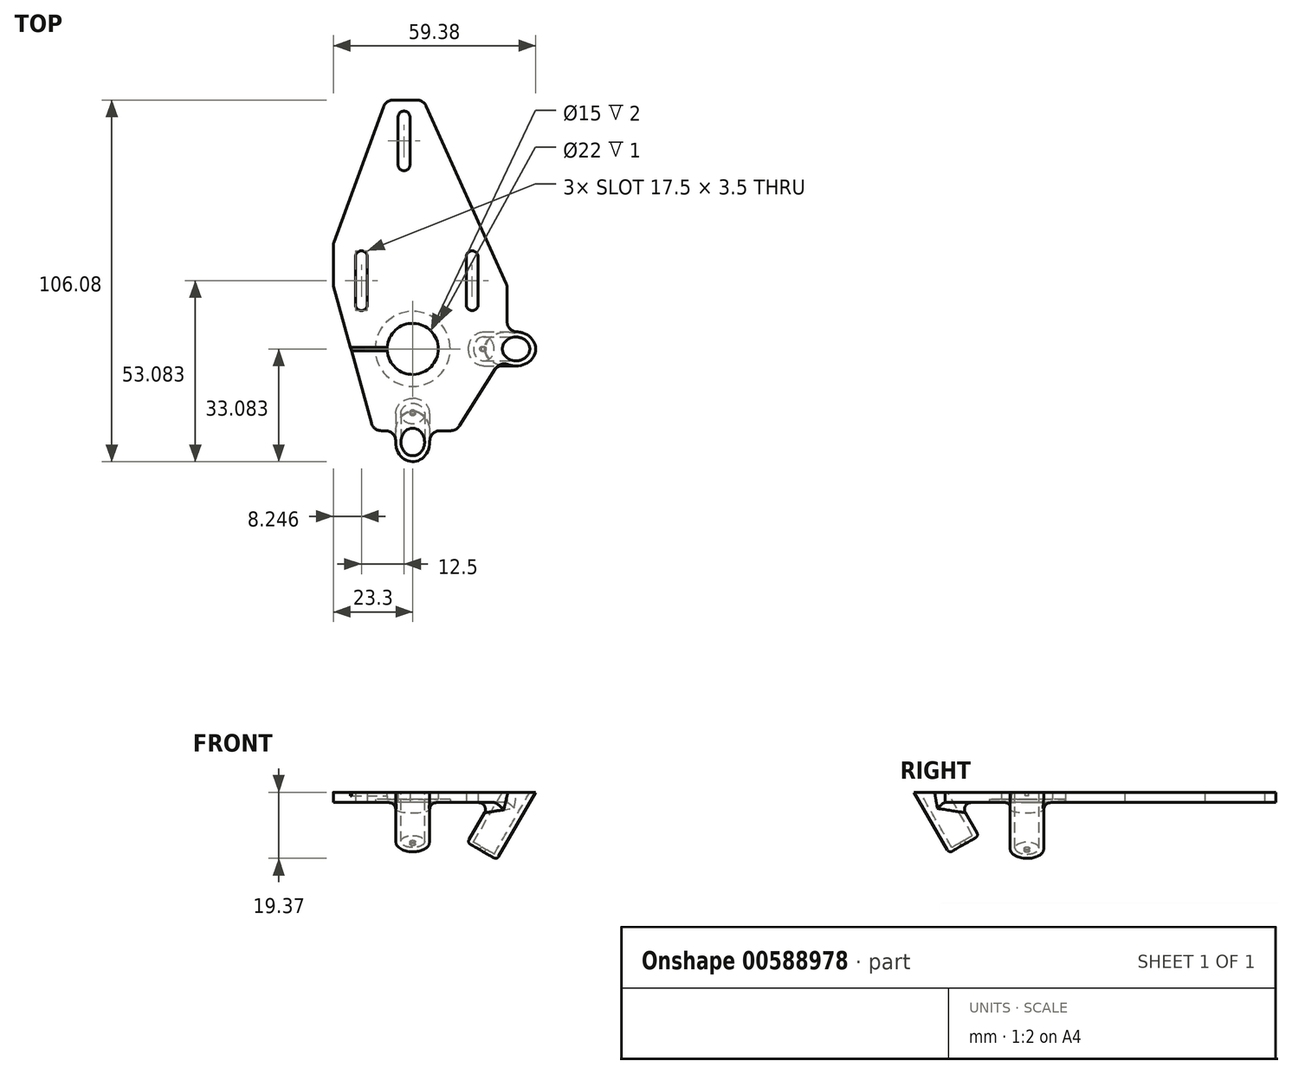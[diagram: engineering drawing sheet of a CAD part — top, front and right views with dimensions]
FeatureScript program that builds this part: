
annotation { "Feature Type Name" : "Feature", "Feature Type Description" : "" }
export const myFeature = defineFeature(function(context is Context, id is Id, definition is map)
    precondition{}
    {
        {
            var Q0;
            Q0=qCreatedBy(makeId("Top.planeOp"),FACE);
            var sketch = newSketch(context, id + "F0", { "sketchPlane" : qUnion([Q0])});
            skLineSegment(sketch, "E0", {"start": v(-23.76, -35) * mm, "end": v(-1.76, -35) * mm});
            skLineSegment(sketch, "E1", {"start": v(-1.76, -35) * mm, "end": v(14.2, -9.6) * mm});
            skLineSegment(sketch, "E2", {"start": v(14.2, -9.6) * mm, "end": v(14.2, 6.4) * mm});
            skLineSegment(sketch, "E3", {"start": v(14.2, 6.4) * mm, "end": v(-6.32, 52) * mm});
            skLineSegment(sketch, "E4", {"start": v(-6.32, 52) * mm, "end": v(-17.32, 52) * mm});
            skLineSegment(sketch, "E5", {"start": v(-17.32, 52) * mm, "end": v(-32.8, 9.74) * mm});
            skLineSegment(sketch, "E6", {"start": v(-32.8, 9.74) * mm, "end": v(-32.8, -2.23) * mm});
            skLineSegment(sketch, "E7", {"start": v(-32.8, -2.23) * mm, "end": v(-23.76, -35) * mm});
            skLineSegment(sketch, "E8", {"start": v(-32.8, 3.75) * mm, "end": v(14.2, 3.75) * mm, "construction": true});
            skLineSegment(sketch, "E9", {"start": v(-12.6, -35) * mm, "end": v(-12.6, 52) * mm, "construction": true});
            skCircle(sketch, "E10", {"center": v(-9.5, -21) * mm, "radius": 7.5 * mm});
            skLineSegment(sketch, "E11.bottom", {"start": v(-26.3, 6) * mm, "end": v(-22.8, 6) * mm});
            skLineSegment(sketch, "E11.top", {"start": v(-26.3, -8) * mm, "end": v(-22.8, -8) * mm});
            skLineSegment(sketch, "E11.left", {"start": v(-26.3, 6) * mm, "end": v(-26.3, -8) * mm});
            skLineSegment(sketch, "E11.right", {"start": v(-22.8, 6) * mm, "end": v(-22.8, -8) * mm});
            skLineSegment(sketch, "E12.bottom", {"start": v(6.2, -8) * mm, "end": v(9.7, -8) * mm});
            skLineSegment(sketch, "E12.top", {"start": v(6.2, 6) * mm, "end": v(9.7, 6) * mm});
            skLineSegment(sketch, "E12.left", {"start": v(6.2, -8) * mm, "end": v(6.2, 6) * mm});
            skLineSegment(sketch, "E12.right", {"start": v(9.7, -8) * mm, "end": v(9.7, 6) * mm});
            skLineSegment(sketch, "E13.bottom", {"start": v(-13.8, 47) * mm, "end": v(-10.3, 47) * mm});
            skLineSegment(sketch, "E13.top", {"start": v(-13.8, 33) * mm, "end": v(-10.3, 33) * mm});
            skLineSegment(sketch, "E13.left", {"start": v(-13.8, 47) * mm, "end": v(-13.8, 33) * mm});
            skLineSegment(sketch, "E13.right", {"start": v(-10.3, 47) * mm, "end": v(-10.3, 33) * mm});
            skArc(sketch, "E14", {"start": v(-10.3, 47) * mm, "mid": v(-12.05, 48.74) * mm, "end": v(-13.8, 47) * mm});
            skArc(sketch, "E15", {"start": v(-13.8, 33) * mm, "mid": v(-12.05, 31.24) * mm, "end": v(-10.3, 33) * mm});
            skArc(sketch, "E16", {"start": v(-22.8, 6) * mm, "mid": v(-24.55, 7.74) * mm, "end": v(-26.3, 6) * mm});
            skArc(sketch, "E17", {"start": v(9.7, 6) * mm, "mid": v(7.95, 7.74) * mm, "end": v(6.2, 6) * mm});
            skArc(sketch, "E18", {"start": v(-26.3, -8) * mm, "mid": v(-24.55, -9.76) * mm, "end": v(-22.8, -8) * mm});
            skArc(sketch, "E19", {"start": v(6.2, -8) * mm, "mid": v(7.95, -9.76) * mm, "end": v(9.7, -8) * mm});
            skLineSegment(sketch, "E20", {"start": v(-32.8, 9.74) * mm, "end": v(-32.8, 64.13) * mm, "construction": true});
            skCircle(sketch, "E21", {"center": v(-9.5, -21) * mm, "radius": 11 * mm});
            skLineSegment(sketch, "E22", {"start": v(14.2, -9.6) * mm, "end": v(14.2, -35) * mm});
            skLineSegment(sketch, "E23", {"start": v(14.2, -35) * mm, "end": v(-1.76, -35) * mm});
            skLineSegment(sketch, "E24", {"start": v(-9.5, -21) * mm, "end": v(55.84, -21) * mm, "construction": true});
            skLineSegment(sketch, "E25", {"start": v(-9.5, -21) * mm, "end": v(-9.5, -68.26) * mm, "construction": true});
            skLineSegment(sketch, "E26", {"start": v(-23.76, -35) * mm, "end": v(-21, -45) * mm});
            skLineSegment(sketch, "E27", {"start": v(-21, -45) * mm, "end": v(14.2, -45) * mm});
            skLineSegment(sketch, "E28", {"start": v(14.2, -45) * mm, "end": v(14.2, -35) * mm});
            skLineSegment(sketch, "E29", {"start": v(3.34, -45) * mm, "end": v(14.2, -27.72) * mm});
            skLineSegment(sketch, "E30.bottom", {"start": v(-30.55, -20.5) * mm, "end": v(-9.5, -20.5) * mm});
            skLineSegment(sketch, "E30.top", {"start": v(-30.55, -21.5) * mm, "end": v(-9.5, -21.5) * mm});
            skLineSegment(sketch, "E30.left", {"start": v(-30.55, -20.5) * mm, "end": v(-30.55, -21.5) * mm});
            skLineSegment(sketch, "E30.right", {"start": v(-9.5, -20.5) * mm, "end": v(-9.5, -21.5) * mm});
            skLineSegment(sketch, "E31", {"start": v(14.2, -27.72) * mm, "end": v(18.2, -21.35) * mm});
            skLineSegment(sketch, "E32", {"start": v(18.2, -21.35) * mm, "end": v(18.2, -2.5) * mm});
            skLineSegment(sketch, "E33", {"start": v(18.2, -2.5) * mm, "end": v(14.2, 6.4) * mm});
            skSolve(sketch);
        }
        {
            var Q0;
            Q0=makeQuery(id+"F0.imprint","IMPRINT",FACE,{"disambiguationData":[TD([[makeQuery(id+"F0.imprint","IMPRINT",EDGE,{"derivedFrom":sQuery(id+"F0.wireOp",EDGE,"E0")}),1.0]])]});
            var Q1;
            Q1=makeQuery(id+"F0.imprint","IMPRINT",FACE,{"disambiguationData":[TD([[makeQuery(id+"F0.imprint","IMPRINT",EDGE,{"derivedFrom":sQuery(id+"F0.wireOp",EDGE,"E10")}),-1.0]])]});
            var Q2;
            Q2=makeQuery(id+"F0.imprint","IMPRINT",FACE,{"disambiguationData":[TD([[makeQuery(id+"F0.imprint","IMPRINT",EDGE,{"derivedFrom":sQuery(id+"F0.wireOp",EDGE,"E1")}),-1.0]])]});
            var Q3;
            Q3=makeQuery(id+"F0.imprint","IMPRINT",FACE,{"disambiguationData":[TD([[makeQuery(id+"F0.imprint","IMPRINT",EDGE,{"derivedFrom":sQuery(id+"F0.wireOp",EDGE,"E0")}),-1.0]])]});
            var Q4;
            {var subQ0=sQuery(id+"F0.wireOp",EDGE,"E30.bottom");var subQ1=sQuery(id+"F0.wireOp",EDGE,"E7");var subQ2=makeQuery(id+"F0.imprint","INTERSECT",VERTEX,{"derivedFrom":[subQ1,subQ0]});Q4=makeQuery(id+"F0.imprint","IMPRINT",FACE,{"disambiguationData":[TD([[makeQuery(id+"F0.imprint","IMPRINT",EDGE,{"disambiguationData":[TD([[subQ2,-1.0]])],"derivedFrom":subQ1}),1.0]])]});}
            var Q5;
            {var subQ2=sQuery(id+"F0.wireOp",EDGE,"E2");Q5=makeQuery(id+"F0.imprint","IMPRINT",FACE,{"disambiguationData":[TD([[makeQuery(id+"F0.imprint","IMPRINT",EDGE,{"derivedFrom":subQ2}),-1.0]])]});}
            extrude(context, id + "F1", {"entities" : qUnion([Q0, Q1, Q2, Q3, Q4, Q5]), "depth" : 3 * mm, "offsetDistance" : 25 * mm});
        }
        {
            var Q0;
            Q0=makeQuery(id+"F0.imprint","IMPRINT",FACE,{"disambiguationData":[TD([[makeQuery(id+"F0.imprint","IMPRINT",EDGE,{"derivedFrom":sQuery(id+"F0.wireOp",EDGE,"E10")}),-1.0]])]});
            extrude(context, id + "F2", {"entities" : qUnion([Q0]), "operationType" : NewBodyOperationType.REMOVE, "depth" : 1 * mm, "offsetDistance" : 25 * mm});
        }
        {
            var Q0;
            Q0=qCreatedBy(makeId("Top.planeOp"),FACE);
            cPlane(context, id + "F3", {"entities" : qUnion([Q0]), "cplaneType" : CPlaneType.OFFSET, "offset" : 49.5 * mm, "oppositeDirection" : true, "width" : 150 * mm, "height" : 150 * mm});
        }
        {
            var Q0;
            Q0=qCreatedBy(id+"F3.planeOp",FACE);
            var sketch = newSketch(context, id + "F4", { "sketchPlane" : qUnion([Q0])});
            skPoint(sketch, "E34", {"position": v(-9.5, -21) * mm});
            skPoint(sketch, "E35", {"position": v(-9.5, -18) * mm});
            skSolve(sketch);
        }
        {
            var Q0;
            Q0=sQuery(id+"F0.wireOp",EDGE,"E32");
            cPlane(context, id + "F5", {"entities" : qUnion([Q0]), "cplaneType" : CPlaneType.LINE_ANGLE, "offset" : 25 * mm, "angle" : 30 * degree, "width" : 150 * mm, "height" : 150 * mm});
        }
        {
            var Q0;
            Q0=makeQuery(id+"F1.opExtrude","CAP_EDGE",EDGE,{"disambiguationData":[OSD([sQuery(id+"F0.wireOp",EDGE,"E27")])],"isStart":false});
            cPlane(context, id + "F6", {"entities" : qUnion([Q0]), "cplaneType" : CPlaneType.LINE_ANGLE, "offset" : 25 * mm, "angle" : 60 * degree, "oppositeDirection" : true, "width" : 150 * mm, "height" : 150 * mm});
        }
        {
            var Q0;
            Q0=qCreatedBy(id+"F6.planeOp",FACE);
            var sketch = newSketch(context, id + "F7", { "sketchPlane" : qUnion([Q0])});
            skCircle(sketch, "E36", {"center": v(-9.5, 40.34) * mm, "radius": 3.5 * mm});
            skCircle(sketch, "E37", {"center": v(-9.5, 40.34) * mm, "radius": 5 * mm});
            skSolve(sketch);
        }
        {
            var Q0;
            Q0=qCreatedBy(id+"F5.planeOp",FACE);
            var sketch = newSketch(context, id + "F8", { "sketchPlane" : qUnion([Q0])});
            skCircle(sketch, "E38", {"center": v(16.52, -21) * mm, "radius": 3.5 * mm});
            skCircle(sketch, "E39", {"center": v(16.52, -21) * mm, "radius": 5 * mm});
            skSolve(sketch);
        }
        {
            var Q0;
            Q0=makeQuery(id+"F7.imprint","IMPRINT",FACE,{"disambiguationData":[TD([[makeQuery(id+"F7.imprint","IMPRINT",EDGE,{"derivedFrom":sQuery(id+"F7.wireOp",EDGE,"E36")}),-1.0]])]});
            extrude(context, id + "F9", {"entities" : qUnion([Q0]), "operationType" : NewBodyOperationType.ADD, "depth" : 15 * mm, "offsetDistance" : 25 * mm});
        }
        {
            var Q0;
            Q0=makeQuery(id+"F8.imprint","IMPRINT",FACE,{"disambiguationData":[TD([[makeQuery(id+"F8.imprint","IMPRINT",EDGE,{"derivedFrom":sQuery(id+"F8.wireOp",EDGE,"E38")}),-1.0]])]});
            extrude(context, id + "F10", {"entities" : qUnion([Q0]), "operationType" : NewBodyOperationType.ADD, "oppositeDirection" : true, "depth" : 15 * mm, "offsetDistance" : 25 * mm});
        }
        {
            var Q0;
            Q0=makeQuery(id+"F7.imprint","IMPRINT",FACE,{"disambiguationData":[TD([[makeQuery(id+"F7.imprint","IMPRINT",EDGE,{"derivedFrom":sQuery(id+"F7.wireOp",EDGE,"E36")}),1.0]])]});
            extrude(context, id + "F11", {"entities" : qUnion([Q0]), "operationType" : NewBodyOperationType.REMOVE, "depth" : 10 * mm, "offsetDistance" : 25 * mm});
        }
        {
            var Q0;
            Q0=makeQuery(id+"F8.imprint","IMPRINT",FACE,{"disambiguationData":[TD([[makeQuery(id+"F8.imprint","IMPRINT",EDGE,{"derivedFrom":sQuery(id+"F8.wireOp",EDGE,"E38")}),1.0]])]});
            extrude(context, id + "F12", {"entities" : qUnion([Q0]), "operationType" : NewBodyOperationType.REMOVE, "oppositeDirection" : true, "depth" : 5 * mm, "offsetDistance" : 25 * mm});
        }
        {
            var Q0;
            Q0=makeQuery(id+"F10.opExtrude","CAP_FACE",FACE,{"disambiguationData":[OSD([sQuery(id+"F8.wireOp",EDGE,"E38"),sQuery(id+"F8.wireOp",EDGE,"E39")])],"isStart":true});
            var Q1;
            Q1=makeQuery(id+"F8.imprint","IMPRINT",FACE,{"disambiguationData":[TD([[makeQuery(id+"F8.imprint","IMPRINT",EDGE,{"derivedFrom":sQuery(id+"F8.wireOp",EDGE,"E38")}),-1.0]])]});
            extrude(context, id + "F13", {"entities" : qUnion([Q0, Q1]), "operationType" : NewBodyOperationType.ADD, "depth" : 7 * mm, "offsetDistance" : 25 * mm});
        }
        {
            var Q0;
            Q0=makeQuery(id+"F9.opExtrude","CAP_FACE",FACE,{"disambiguationData":[OSD([sQuery(id+"F7.wireOp",EDGE,"E36"),sQuery(id+"F7.wireOp",EDGE,"E37")])],"isStart":true});
            extrude(context, id + "F14", {"entities" : qUnion([Q0]), "operationType" : NewBodyOperationType.ADD, "depth" : 5 * mm, "offsetDistance" : 25 * mm});
        }
        {
            var Q0;
            Q0=makeQuery(id+"F1.opExtrude","SWEPT_FACE",FACE,{"disambiguationData":[OSD([sQuery(id+"F0.wireOp",EDGE,"E7"),sQuery(id+"F0.wireOp",EDGE,"E26")])]});
            var sketch = newSketch(context, id + "F15", { "sketchPlane" : qUnion([Q0])});
            skLineSegment(sketch, "E40.bottom", {"start": v(-6.57, 3) * mm, "end": v(71.8, 3) * mm});
            skLineSegment(sketch, "E40.top", {"start": v(-6.57, 11.39) * mm, "end": v(71.8, 11.39) * mm});
            skLineSegment(sketch, "E40.left", {"start": v(-6.57, 3) * mm, "end": v(-6.57, 11.39) * mm});
            skLineSegment(sketch, "E40.right", {"start": v(71.8, 3) * mm, "end": v(71.8, 11.39) * mm});
            skSolve(sketch);
        }
        {
            var Q0;
            Q0=makeQuery(id+"F15.imprint","IMPRINT",FACE,{"disambiguationData":[TD([[makeQuery(id+"F15.imprint","IMPRINT",EDGE,{"derivedFrom":sQuery(id+"F15.wireOp",EDGE,"E40.top")}),-1.0]])]});
            extrude(context, id + "F16", {"entities" : qUnion([Q0]), "operationType" : NewBodyOperationType.REMOVE, "oppositeDirection" : true, "depth" : 60 * mm, "offsetDistance" : 25 * mm});
        }
        {
            var Q0;
            Q0=makeQuery(id+"F10.opExtrude","CAP_FACE",FACE,{"disambiguationData":[OSD([sQuery(id+"F8.wireOp",EDGE,"E38"),sQuery(id+"F8.wireOp",EDGE,"E39")])],"isStart":false});
            var sketch = newSketch(context, id + "F17", { "sketchPlane" : qUnion([Q0])});
            skCircle(sketch, "E41", {"center": v(16.52, 21) * mm, "radius": 5 * mm});
            skCircle(sketch, "E42", {"center": v(16.52, 21) * mm, "radius": 0.75 * mm});
            skSolve(sketch);
        }
        {
            var Q0;
            Q0=makeQuery(id+"F17.imprint","IMPRINT",FACE,{"disambiguationData":[TD([[makeQuery(id+"F17.imprint","IMPRINT",EDGE,{"derivedFrom":sQuery(id+"F17.wireOp",EDGE,"E42")}),-1.0]])]});
            var Q1;
            Q1=makeQuery(id+"F17.imprint","IMPRINT",FACE,{"disambiguationData":[TD([[makeQuery(id+"F17.imprint","IMPRINT",EDGE,{"derivedFrom":sQuery(id+"F17.wireOp",EDGE,"E41")}),-1.0]])]});
            extrude(context, id + "F18", {"entities" : qUnion([Q0, Q1]), "operationType" : NewBodyOperationType.ADD, "depth" : 1 * mm, "offsetDistance" : 25 * mm});
        }
        {
            var Q0;
            Q0=makeQuery(id+"F9.opExtrude","CAP_FACE",FACE,{"disambiguationData":[OSD([sQuery(id+"F7.wireOp",EDGE,"E36"),sQuery(id+"F7.wireOp",EDGE,"E37")])],"isStart":false});
            var sketch = newSketch(context, id + "F19", { "sketchPlane" : qUnion([Q0])});
            skCircle(sketch, "E43", {"center": v(-9.5, 40.34) * mm, "radius": 5 * mm});
            skCircle(sketch, "E44", {"center": v(-9.5, 40.34) * mm, "radius": 0.75 * mm});
            skSolve(sketch);
        }
        {
            var Q0;
            Q0=makeQuery(id+"F19.imprint","IMPRINT",FACE,{"disambiguationData":[TD([[makeQuery(id+"F19.imprint","IMPRINT",EDGE,{"derivedFrom":sQuery(id+"F19.wireOp",EDGE,"E44")}),-1.0]])]});
            var Q1;
            Q1=makeQuery(id+"F19.imprint","IMPRINT",FACE,{"disambiguationData":[TD([[makeQuery(id+"F19.imprint","IMPRINT",EDGE,{"derivedFrom":sQuery(id+"F19.wireOp",EDGE,"E43")}),1.0]])]});
            extrude(context, id + "F20", {"entities" : qUnion([Q0, Q1]), "operationType" : NewBodyOperationType.ADD, "depth" : 1 * mm, "offsetDistance" : 25 * mm});
        }
        {
            var Q0;
            Q0=makeQuery(id+"F1.opExtrude","SWEPT_EDGE",EDGE,{"disambiguationData":[OSD([sQuery(id+"F0.wireOp",EDGE,"E27"),sQuery(id+"F0.wireOp",EDGE,"E29")])]});
            var Q1;
            Q1=makeQuery(id+"F1.opExtrude","SWEPT_EDGE",EDGE,{"disambiguationData":[OSD([sQuery(id+"F0.wireOp",EDGE,"E26"),sQuery(id+"F0.wireOp",EDGE,"E27")])]});
            var Q2;
            Q2=makeQuery(id+"F1.opExtrude","SWEPT_EDGE",EDGE,{"disambiguationData":[OSD([sQuery(id+"F0.wireOp",EDGE,"E22"),sQuery(id+"F0.wireOp",EDGE,"E29")])]});
            var Q3;
            Q3=makeQuery(id+"F1.opExtrude","SWEPT_EDGE",EDGE,{"disambiguationData":[OSD([sQuery(id+"F0.wireOp",EDGE,"E6"),sQuery(id+"F0.wireOp",EDGE,"E7")])]});
            var Q4;
            Q4=makeQuery(id+"F1.opExtrude","SWEPT_EDGE",EDGE,{"disambiguationData":[OSD([sQuery(id+"F0.wireOp",EDGE,"E2"),sQuery(id+"F0.wireOp",EDGE,"E3")])]});
            var Q5;
            Q5=makeQuery(id+"F1.opExtrude","SWEPT_EDGE",EDGE,{"disambiguationData":[OSD([sQuery(id+"F0.wireOp",EDGE,"E3"),sQuery(id+"F0.wireOp",EDGE,"E4")])]});
            var Q6;
            Q6=makeQuery(id+"F1.opExtrude","SWEPT_EDGE",EDGE,{"disambiguationData":[OSD([sQuery(id+"F0.wireOp",EDGE,"E4"),sQuery(id+"F0.wireOp",EDGE,"E5")])]});
            var Q7;
            Q7=makeQuery(id+"F1.opExtrude","SWEPT_EDGE",EDGE,{"disambiguationData":[OSD([sQuery(id+"F0.wireOp",EDGE,"E5"),sQuery(id+"F0.wireOp",EDGE,"E6")])]});
            var Q8;
            Q8=makeQuery(id+"F1.opExtrude","SWEPT_EDGE",EDGE,{"disambiguationData":[OSD([sQuery(id+"F0.wireOp",EDGE,"E32"),sQuery(id+"F0.wireOp",EDGE,"E33")])]});
            var Q9;
            {var subQ0=sQuery(id+"F8.wireOp",EDGE,"E39");Q9=makeQuery(id+"F13.boolean.opBoolean","INTERSECT",EDGE,{"derivedFrom":[makeQuery(id+"F1.opExtrude","SWEPT_FACE",FACE,{"disambiguationData":[OSD([sQuery(id+"F0.wireOp",EDGE,"E32")])]}),makeQuery(id+"F13.opExtrude","SWEPT_FACE",FACE,{"disambiguationData":[OSD([subQ0]),TDD([makeQuery(id+"F8.imprint","IMPRINT",EDGE,{"derivedFrom":subQ0})])]})]});}
            var Q10;
            {var subQ0=sQuery(id+"F8.wireOp",EDGE,"E39");Q10=makeQuery(id+"F13.boolean.opBoolean","INTERSECT",EDGE,{"derivedFrom":[makeQuery(id+"F1.opExtrude","SWEPT_FACE",FACE,{"disambiguationData":[OSD([sQuery(id+"F0.wireOp",EDGE,"E29"),sQuery(id+"F0.wireOp",EDGE,"E31")])]}),makeQuery(id+"F13.opExtrude","SWEPT_FACE",FACE,{"disambiguationData":[OSD([subQ0]),TDD([makeQuery(id+"F8.imprint","IMPRINT",EDGE,{"derivedFrom":subQ0})])]})]});}
            var Q11;
            Q11=makeQuery(id+"F9.boolean.opBoolean","INTERSECT",EDGE,{"disambiguationData":[OD(1.0)],"derivedFrom":[makeQuery(id+"F1.opExtrude","SWEPT_FACE",FACE,{"disambiguationData":[OSD([sQuery(id+"F0.wireOp",EDGE,"E27")])]}),makeQuery(id+"F9.opExtrude","SWEPT_FACE",FACE,{"disambiguationData":[OSD([sQuery(id+"F7.wireOp",EDGE,"E37")])]})]});
            var Q12;
            Q12=makeQuery(id+"F9.boolean.opBoolean","INTERSECT",EDGE,{"disambiguationData":[OD(0.0)],"derivedFrom":[makeQuery(id+"F1.opExtrude","SWEPT_FACE",FACE,{"disambiguationData":[OSD([sQuery(id+"F0.wireOp",EDGE,"E27")])]}),makeQuery(id+"F9.opExtrude","SWEPT_FACE",FACE,{"disambiguationData":[OSD([sQuery(id+"F7.wireOp",EDGE,"E37")])]})]});
            fillet(context, id + "F21", {"entities" : qUnion([Q0, Q1, Q2, Q3, Q4, Q5, Q6, Q7, Q8, Q9, Q10, Q11, Q12]), "radius" : 3 * mm, "tangentPropagation" : true, "allowEdgeOverflow" : false});
        }
        {
            var Q0;
            {var subQ0=sQuery(id+"F0.wireOp",EDGE,"E12.right");var subQ1=sQuery(id+"F0.wireOp",EDGE,"E12.left");var subQ2=sQuery(id+"F0.wireOp",EDGE,"E11.right");var subQ3=sQuery(id+"F0.wireOp",EDGE,"E11.left");var subQ4=sQuery(id+"F0.wireOp",EDGE,"E26");var subQ5=sQuery(id+"F0.wireOp",EDGE,"E7");var subQ6=sQuery(id+"F0.wireOp",EDGE,"E6");var subQ7=sQuery(id+"F0.wireOp",EDGE,"E22");var subQ8=sQuery(id+"F0.wireOp",EDGE,"E2");var subQ9=sQuery(id+"F0.wireOp",EDGE,"E3");var subQ10=sQuery(id+"F0.wireOp",EDGE,"E4");var subQ11=sQuery(id+"F0.wireOp",EDGE,"E5");var subQ12=sQuery(id+"F0.wireOp",EDGE,"E13.left");var subQ13=sQuery(id+"F0.wireOp",EDGE,"E13.right");var subQ14=sQuery(id+"F0.wireOp",EDGE,"E14");var subQ15=sQuery(id+"F0.wireOp",EDGE,"E15");var subQ16=sQuery(id+"F0.wireOp",EDGE,"E16");var subQ17=sQuery(id+"F0.wireOp",EDGE,"E17");var subQ18=sQuery(id+"F0.wireOp",EDGE,"E18");var subQ19=sQuery(id+"F0.wireOp",EDGE,"E19");var subQ20=sQuery(id+"F0.wireOp",EDGE,"E27");var subQ21=sQuery(id+"F0.wireOp",EDGE,"E29");Q0=makeQuery(id+"F10.boolean.opBoolean","INTERSECT",EDGE,{"derivedFrom":[makeQuery(id+"F9.boolean.opBoolean","SPLIT",FACE,{"disambiguationData":[TD([makeQuery(id+"F1.opExtrude","SWEPT_FACE",FACE,{"disambiguationData":[OSD([subQ9])]})])],"derivedFrom":makeQuery(id+"F1.opExtrude","CAP_FACE",FACE,{"disambiguationData":[OSD([subQ8,subQ9,subQ10,subQ11,subQ6,subQ5,sQuery(id+"F0.wireOp",EDGE,"E10"),subQ3,subQ2,subQ1,subQ0,subQ12,subQ13,subQ14,subQ15,subQ16,subQ17,subQ18,subQ19,subQ7,subQ4,subQ20,subQ21])],"isStart":true})}),makeQuery(id+"F10.opExtrude","SWEPT_FACE",FACE,{"disambiguationData":[OSD([sQuery(id+"F8.wireOp",EDGE,"E39")])]})]});}
            var Q1;
            Q1=makeQuery(id+"F9.boolean.opBoolean","INTERSECT",EDGE,{"derivedFrom":[makeQuery(id+"F1.opExtrude","CAP_FACE",FACE,{"disambiguationData":[OSD([sQuery(id+"F0.wireOp",EDGE,"E2"),sQuery(id+"F0.wireOp",EDGE,"E3"),sQuery(id+"F0.wireOp",EDGE,"E4"),sQuery(id+"F0.wireOp",EDGE,"E5"),sQuery(id+"F0.wireOp",EDGE,"E6"),sQuery(id+"F0.wireOp",EDGE,"E7"),sQuery(id+"F0.wireOp",EDGE,"E10"),sQuery(id+"F0.wireOp",EDGE,"E11.left"),sQuery(id+"F0.wireOp",EDGE,"E11.right"),sQuery(id+"F0.wireOp",EDGE,"E12.left"),sQuery(id+"F0.wireOp",EDGE,"E12.right"),sQuery(id+"F0.wireOp",EDGE,"E13.left"),sQuery(id+"F0.wireOp",EDGE,"E13.right"),sQuery(id+"F0.wireOp",EDGE,"E14"),sQuery(id+"F0.wireOp",EDGE,"E15"),sQuery(id+"F0.wireOp",EDGE,"E16"),sQuery(id+"F0.wireOp",EDGE,"E17"),sQuery(id+"F0.wireOp",EDGE,"E18"),sQuery(id+"F0.wireOp",EDGE,"E19"),sQuery(id+"F0.wireOp",EDGE,"E22"),sQuery(id+"F0.wireOp",EDGE,"E26"),sQuery(id+"F0.wireOp",EDGE,"E27"),sQuery(id+"F0.wireOp",EDGE,"E29")])],"isStart":true}),makeQuery(id+"F9.opExtrude","SWEPT_FACE",FACE,{"disambiguationData":[OSD([sQuery(id+"F7.wireOp",EDGE,"E37")])]})]});
            fillet(context, id + "F22", {"entities" : qUnion([Q0, Q1]), "radius" : 2 * mm, "tangentPropagation" : true, "allowEdgeOverflow" : false});
        }
        {
            var Q0;
            Q0=makeQuery(id+"F20.opExtrude","CAP_EDGE",EDGE,{"disambiguationData":[OSD([sQuery(id+"F19.wireOp",EDGE,"E43")])],"isStart":false});
            var Q1;
            Q1=makeQuery(id+"F18.opExtrude","CAP_EDGE",EDGE,{"disambiguationData":[OSD([sQuery(id+"F17.wireOp",EDGE,"E41")])],"isStart":false});
            fillet(context, id + "F23", {"entities" : qUnion([Q0, Q1]), "radius" : 1 * mm, "tangentPropagation" : true, "allowEdgeOverflow" : false});
        }
        {
            var Q0;
            {var subQ0=sQuery(id+"F0.wireOp",EDGE,"E29");var subQ2=sQuery(id+"F0.wireOp",EDGE,"E27");var subQ4=sQuery(id+"F0.wireOp",EDGE,"E19");var subQ6=sQuery(id+"F0.wireOp",EDGE,"E18");var subQ8=sQuery(id+"F0.wireOp",EDGE,"E17");var subQ10=sQuery(id+"F0.wireOp",EDGE,"E16");var subQ12=sQuery(id+"F0.wireOp",EDGE,"E15");var subQ14=sQuery(id+"F0.wireOp",EDGE,"E14");var subQ16=sQuery(id+"F0.wireOp",EDGE,"E13.right");var subQ18=sQuery(id+"F0.wireOp",EDGE,"E13.left");var subQ20=sQuery(id+"F0.wireOp",EDGE,"E12.right");var subQ22=sQuery(id+"F0.wireOp",EDGE,"E5");var subQ24=sQuery(id+"F0.wireOp",EDGE,"E4");var subQ26=sQuery(id+"F0.wireOp",EDGE,"E3");var subQ27=makeQuery(id+"F1.opExtrude","SWEPT_FACE",FACE,{"disambiguationData":[OSD([subQ26])]});var subQ28=sQuery(id+"F0.wireOp",EDGE,"E22");var subQ29=sQuery(id+"F0.wireOp",EDGE,"E2");var subQ31=sQuery(id+"F0.wireOp",EDGE,"E6");var subQ33=sQuery(id+"F0.wireOp",EDGE,"E26");var subQ34=sQuery(id+"F0.wireOp",EDGE,"E7");var subQ38=sQuery(id+"F0.wireOp",EDGE,"E10");var subQ40=sQuery(id+"F0.wireOp",EDGE,"E11.left");var subQ42=sQuery(id+"F0.wireOp",EDGE,"E11.right");var subQ44=sQuery(id+"F0.wireOp",EDGE,"E12.left");Q0=makeQuery(id+"F16.boolean.opBoolean","MERGE",FACE,{"derivedFrom":[makeQuery(id+"F10.boolean.opBoolean","SPLIT",FACE,{"disambiguationData":[TD([subQ27])],"derivedFrom":makeQuery(id+"F9.boolean.opBoolean","SPLIT",FACE,{"disambiguationData":[TD([subQ27])],"derivedFrom":makeQuery(id+"F1.opExtrude","CAP_FACE",FACE,{"disambiguationData":[OSD([subQ29,subQ26,subQ24,subQ22,subQ31,subQ34,subQ38,subQ40,subQ42,subQ44,subQ20,subQ18,subQ16,subQ14,subQ12,subQ10,subQ8,subQ6,subQ4,subQ28,subQ33,subQ2,subQ0])],"isStart":false})})}),makeQuery(id+"F16.opExtrude","SWEPT_FACE",FACE,{"disambiguationData":[OSD([sQuery(id+"F15.wireOp",EDGE,"E40.bottom")])]})]});}
            var sketch = newSketch(context, id + "F24", { "sketchPlane" : qUnion([Q0])});
            skLineSegment(sketch, "E45.bottom", {"start": v(-30.55, -20.5) * mm, "end": v(-9.5, -20.5) * mm});
            skLineSegment(sketch, "E45.top", {"start": v(-30.55, -21.5) * mm, "end": v(-9.5, -21.5) * mm});
            skLineSegment(sketch, "E45.left", {"start": v(-30.55, -20.5) * mm, "end": v(-30.55, -21.5) * mm});
            skLineSegment(sketch, "E45.right", {"start": v(-9.5, -20.5) * mm, "end": v(-9.5, -21.5) * mm});
            skSolve(sketch);
        }
        {
            var Q0;
            {var subQ0=sQuery(id+"F24.wireOp",EDGE,"E45.bottom");var subQ3=makeQuery(id+"F1.opExtrude","CAP_EDGE",EDGE,{"disambiguationData":[OSD([sQuery(id+"F0.wireOp",EDGE,"E10")])],"isStart":false});var subQ4=makeQuery(id+"F24.imprint","INTERSECT",VERTEX,{"derivedFrom":[subQ3,subQ0]});Q0=makeQuery(id+"F24.imprint","IMPRINT",FACE,{"disambiguationData":[TD([[makeQuery(id+"F24.imprint","IMPRINT",EDGE,{"disambiguationData":[TD([[subQ4,-1.0]])],"derivedFrom":subQ3}),-1.0]])]});}
            extrude(context, id + "F25", {"entities" : qUnion([Q0]), "operationType" : NewBodyOperationType.REMOVE, "oppositeDirection" : true, "depth" : 1 * mm, "offsetDistance" : 25 * mm});
        }
        {
            var Q0;
            Q0=makeQuery(id+"F8.imprint","IMPRINT",FACE,{"disambiguationData":[TD([[makeQuery(id+"F8.imprint","IMPRINT",EDGE,{"derivedFrom":sQuery(id+"F8.wireOp",EDGE,"E38")}),1.0]])]});
            extrude(context, id + "F26", {"entities" : qUnion([Q0]), "operationType" : NewBodyOperationType.REMOVE, "depth" : 5 * mm, "offsetDistance" : 25 * mm});
        }
    });
